# Revit family: Screens-Mounted-Teknion-JNSAGW-Glass_Add-On-R2015
name_source: partatom
category: Furniture
revit_build: Autodesk Revit Architecture 2015 (Build: 20140323_1530(x64)
units: mm (PartAtom-declared; Revit-internal decimal feet)

## types (3) — shared parameters
Assembly Code = E2020200
Manufacturer = Teknion
Manufacturer Fax = 416.661.4586
Part Number = JNSAGW
Product Documentation Link = http://www.teknion.com
Product Line = Expansion Cityline
Product Page URL = http://www.teknion.com
Series = Expansion Cityline
Sustainability Data = http://www.teknion.com
URL = www.teknion.com
Unit Weight URL = http://www.teknion.com
Warranty = http://www.teknion.com

## per-type parameters (varying)
| type | Description | Model |
| Standard Width | Glass Add-On Screen – Desk-Mounted, Standard Width, Standard Corner Detail | JNSAGW__SS |
| One Side Shared Screen | Glass Add-On Screen – Desk-Mounted, One Side Shared Screen, Standard Corner Detail | JNSAGW__HS |
| One Side Full Screen or Both Sides Shared Screens | Glass Add-On Screen – Desk-Mounted, One Side Full Screen or Both Sides Shared Screens, Standard Corner Detail | JNSAGW__FS |

type visibility flags: 3 boolean params named "<type name>" — each type sets only its own to Yes (folded from table)

## geometry (parser evidence)
native form markers: Sweep x2
no freeform markers — native parametric forms only
